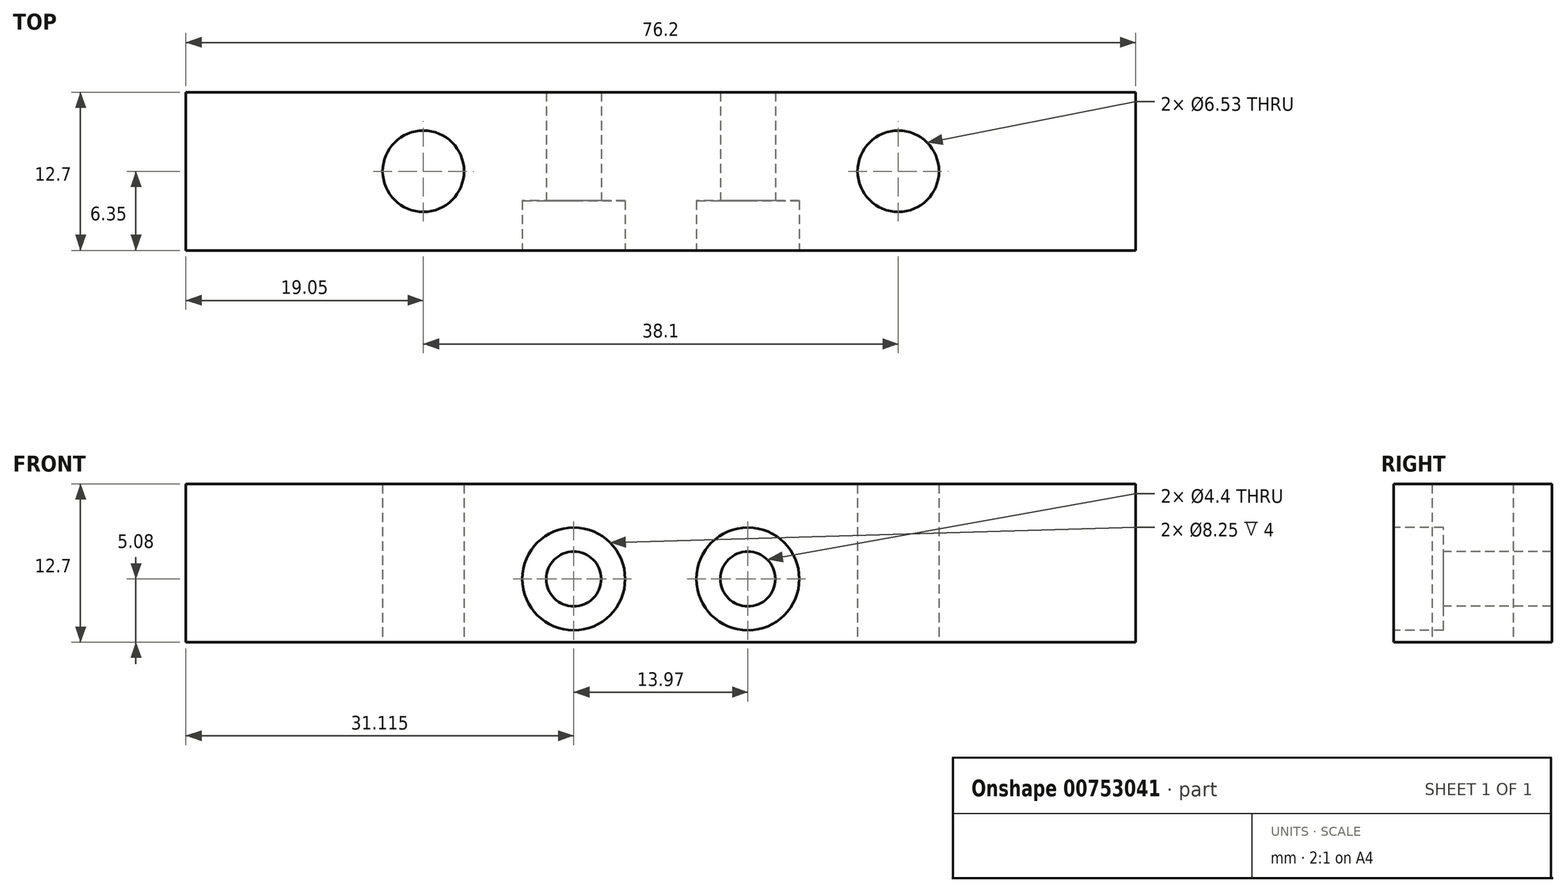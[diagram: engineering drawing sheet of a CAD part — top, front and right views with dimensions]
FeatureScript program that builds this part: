
annotation { "Feature Type Name" : "Feature", "Feature Type Description" : "" }
export const myFeature = defineFeature(function(context is Context, id is Id, definition is map)
    precondition{}
    {
        {
            var Q0;
            Q0=qCreatedBy(makeId("Top.planeOp"),FACE);
            var sketch = newSketch(context, id + "F0", { "sketchPlane" : qUnion([Q0])});
            skLineSegment(sketch, "E0.bottom", {"start": v(38.1, -6.35) * mm, "end": v(-38.1, -6.35) * mm});
            skLineSegment(sketch, "E0.top", {"start": v(38.1, 6.35) * mm, "end": v(-38.1, 6.35) * mm});
            skLineSegment(sketch, "E0.left", {"start": v(38.1, -6.35) * mm, "end": v(38.1, 6.35) * mm});
            skLineSegment(sketch, "E0.right", {"start": v(-38.1, -6.35) * mm, "end": v(-38.1, 6.35) * mm});
            skPoint(sketch, "E0.middle", {"position": v(0, 0) * mm});
            skPoint(sketch, "E1", {"position": v(-19.05, 0) * mm});
            skPoint(sketch, "E2", {"position": v(19.05, 0) * mm});
            skSolve(sketch);
        }
        {
            var Q0;
            Q0=makeQuery(id+"F0.imprint","IMPRINT",FACE,{"disambiguationData":[TD([[makeQuery(id+"F0.imprint","IMPRINT",EDGE,{"derivedFrom":sQuery(id+"F0.wireOp",EDGE,"E0.bottom")}),-1.0]])]});
            extrude(context, id + "F1", {"entities" : qUnion([Q0]), "depth" : 12.7 * mm, "offsetDistance" : 25.4 * mm});
        }
        {
            var Q0;
            Q0=sQuery(id+"F0.wireOp",VERTEX,"E1");
            var Q1;
            Q1=makeQuery(id+"F1.opExtrude","SWEPT_BODY",BODY,{"disambiguationData":[OSD([sQuery(id+"F0.wireOp",EDGE,"E0.bottom"),sQuery(id+"F0.wireOp",EDGE,"E0.top"),sQuery(id+"F0.wireOp",EDGE,"E0.left"),sQuery(id+"F0.wireOp",EDGE,"E0.right")])]});
            hole(context, id + "F2", {"style" : HoleStyle.SIMPLE, "endStyle" : HoleEndStyle.THROUGH, "oppositeDirection" : true, "standardTappedOrClearance" : lookupTablePath({ "standard" : "ANSI", "fit" : "Close", "size" : "1/4", "type" : "Clearance" }), "standardBlindInLast" : lookupTablePath({ "fit" : "Close", "standard" : "ANSI", "size" : "1/4", "type" : "Clearance" }), "holeDiameter" : 6.53 * mm, "majorDiameter" : 6.35 * mm, "isTappedThrough" : true, "tappedDepth" : 25.4 * mm, "tapClearance" : 3, "locations" : qUnion([Q0]), "scope" : qUnion([Q1])});
        }
        {
            var Q0;
            Q0=sQuery(id+"F0.wireOp",VERTEX,"E2");
            var Q1;
            Q1=makeQuery(id+"F1.opExtrude","SWEPT_BODY",BODY,{"disambiguationData":[OSD([sQuery(id+"F0.wireOp",EDGE,"E0.bottom"),sQuery(id+"F0.wireOp",EDGE,"E0.top"),sQuery(id+"F0.wireOp",EDGE,"E0.left"),sQuery(id+"F0.wireOp",EDGE,"E0.right")])]});
            hole(context, id + "F3", {"style" : HoleStyle.SIMPLE, "endStyle" : HoleEndStyle.THROUGH, "oppositeDirection" : true, "standardTappedOrClearance" : lookupTablePath({ "standard" : "ANSI", "fit" : "Close", "size" : "1/4", "type" : "Clearance" }), "standardBlindInLast" : lookupTablePath({ "fit" : "Close", "standard" : "ANSI", "size" : "1/4", "type" : "Clearance" }), "holeDiameter" : 6.53 * mm, "majorDiameter" : 6.35 * mm, "isTappedThrough" : true, "tappedDepth" : 25.4 * mm, "tapClearance" : 3, "startFromSketch" : true, "locations" : qUnion([Q0]), "scope" : qUnion([Q1])});
        }
        {
            var Q0;
            Q0=makeQuery(id+"F1.opExtrude","SWEPT_FACE",FACE,{"disambiguationData":[OSD([sQuery(id+"F0.wireOp",EDGE,"E0.bottom")])]});
            var sketch = newSketch(context, id + "F4", { "sketchPlane" : qUnion([Q0])});
            skPoint(sketch, "E3", {"position": v(-6.99, 5.08) * mm});
            skPoint(sketch, "E4", {"position": v(6.99, 5.08) * mm});
            skSolve(sketch);
        }
        {
            var Q0;
            Q0=sQuery(id+"F4.wireOp",VERTEX,"E3");
            var Q1;
            Q1=makeQuery(id+"F1.opExtrude","SWEPT_BODY",BODY,{"disambiguationData":[OSD([sQuery(id+"F0.wireOp",EDGE,"E0.bottom"),sQuery(id+"F0.wireOp",EDGE,"E0.top"),sQuery(id+"F0.wireOp",EDGE,"E0.left"),sQuery(id+"F0.wireOp",EDGE,"E0.right")])]});
            hole(context, id + "F5", {"style" : HoleStyle.C_BORE, "endStyle" : HoleEndStyle.THROUGH, "standardTappedOrClearance" : lookupTablePath({ "standard" : "ISO", "fit" : "Normal", "size" : "M4", "type" : "Clearance" }), "standardBlindInLast" : lookupTablePath({ "fit" : "Standard", "standard" : "ISO", "size" : "M4", "type" : "Clearance" }), "holeDiameter" : 4.4 * mm, "cBoreDiameter" : 8.25 * mm, "cBoreDepth" : 4 * mm, "majorDiameter" : 6.35 * mm, "isTappedThrough" : true, "tappedDepth" : 25.4 * mm, "tapClearance" : 3, "startFromSketch" : true, "locations" : qUnion([Q0]), "scope" : qUnion([Q1])});
        }
        {
            var Q0;
            Q0=sQuery(id+"F4.wireOp",VERTEX,"E4");
            var Q1;
            Q1=makeQuery(id+"F1.opExtrude","SWEPT_BODY",BODY,{"disambiguationData":[OSD([sQuery(id+"F0.wireOp",EDGE,"E0.bottom"),sQuery(id+"F0.wireOp",EDGE,"E0.top"),sQuery(id+"F0.wireOp",EDGE,"E0.left"),sQuery(id+"F0.wireOp",EDGE,"E0.right")])]});
            hole(context, id + "F6", {"style" : HoleStyle.C_BORE, "endStyle" : HoleEndStyle.THROUGH, "standardTappedOrClearance" : lookupTablePath({ "standard" : "ISO", "fit" : "Normal", "size" : "M4", "type" : "Clearance" }), "standardBlindInLast" : lookupTablePath({ "fit" : "Standard", "standard" : "ISO", "size" : "M4", "type" : "Clearance" }), "holeDiameter" : 4.4 * mm, "cBoreDiameter" : 8.25 * mm, "cBoreDepth" : 4 * mm, "majorDiameter" : 6.35 * mm, "isTappedThrough" : true, "tappedDepth" : 25.4 * mm, "tapClearance" : 3, "startFromSketch" : true, "locations" : qUnion([Q0]), "scope" : qUnion([Q1])});
        }
    });
